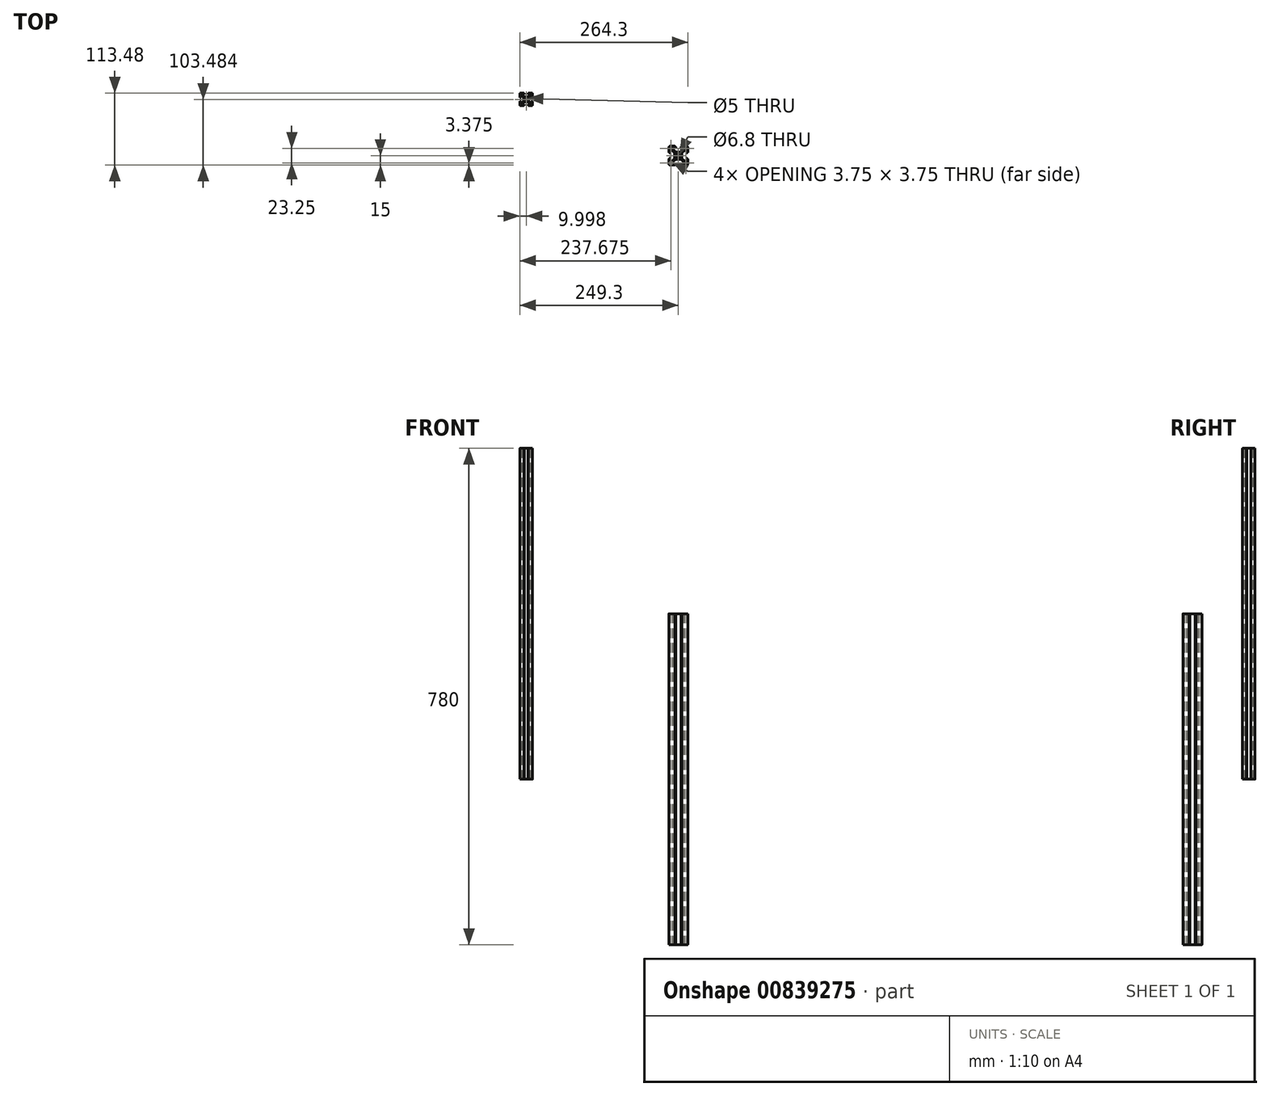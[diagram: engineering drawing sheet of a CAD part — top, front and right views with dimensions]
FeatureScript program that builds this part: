
annotation { "Feature Type Name" : "Feature", "Feature Type Description" : "" }
export const myFeature = defineFeature(function(context is Context, id is Id, definition is map)
    precondition{}
    {
        {
            var Q0;
            Q0=qCreatedBy(makeId("Top.planeOp"),FACE);
            var sketch = newSketch(context, id + "F0", { "sketchPlane" : qUnion([Q0])});
            skLineSegment(sketch, "E0.bottom", {"start": v(12.5, -15) * mm, "end": v(5.2, -15) * mm});
            skLineSegment(sketch, "E0.top", {"start": v(12.5, 15) * mm, "end": v(5.2, 15) * mm});
            skLineSegment(sketch, "E0.left", {"start": v(15, -12.5) * mm, "end": v(15, -5.2) * mm});
            skLineSegment(sketch, "E0.right", {"start": v(-15, -12.5) * mm, "end": v(-15, -5.2) * mm});
            skPoint(sketch, "E0.middle", {"position": v(0, 0) * mm});
            skCircle(sketch, "E1", {"center": v(0, 0) * mm, "radius": 3.4 * mm});
            skLineSegment(sketch, "E2.bottom", {"start": v(4.24, -5.8) * mm, "end": v(-4.24, -5.8) * mm});
            skLineSegment(sketch, "E2.top", {"start": v(4.24, 5.8) * mm, "end": v(-4.24, 5.8) * mm});
            skLineSegment(sketch, "E2.left", {"start": v(5.8, -4.24) * mm, "end": v(5.8, 4.24) * mm});
            skLineSegment(sketch, "E2.right", {"start": v(-5.8, -4.24) * mm, "end": v(-5.8, 4.24) * mm});
            skLineSegment(sketch, "E3.bottom", {"start": v(12.5, 15) * mm, "end": v(8.25, 15) * mm});
            skLineSegment(sketch, "E3.left", {"start": v(15, 12.5) * mm, "end": v(15, 8.25) * mm});
            skLineSegment(sketch, "E3.right", {"start": v(8.25, 12.8) * mm, "end": v(8.25, 9.8) * mm});
            skLineSegment(sketch, "E4.bottom", {"start": v(12.5, 9.75) * mm, "end": v(10.75, 9.75) * mm});
            skLineSegment(sketch, "E4.top", {"start": v(12.5, 13.5) * mm, "end": v(10.75, 13.5) * mm});
            skLineSegment(sketch, "E4.left", {"start": v(13.5, 10.75) * mm, "end": v(13.5, 12.5) * mm});
            skLineSegment(sketch, "E4.right", {"start": v(9.75, 10.75) * mm, "end": v(9.75, 12.5) * mm});
            skPoint(sketch, "E4.middle", {"position": v(11.62, 11.63) * mm});
            skLineSegment(sketch, "E5", {"start": v(9.8, 8.25) * mm, "end": v(5.8, 4.24) * mm});
            skLineSegment(sketch, "E6.MirrorCS", {"start": v(8.25, 9.8) * mm, "end": v(4.24, 5.8) * mm});
            skLineSegment(sketch, "E7", {"start": v(12.8, 8.25) * mm, "end": v(12.8, 4.1) * mm});
            skPoint(sketch, "E8.visualSharp", {"position": v(15, 15) * mm});
            skArc(sketch, "E8.filletArc", {"start": v(15, 12.5) * mm, "mid": v(14.27, 14.27) * mm, "end": v(12.5, 15) * mm});
            skLineSegment(sketch, "E9.MirrorCS", {"start": v(12.8, -8.25) * mm, "end": v(12.8, -4.1) * mm});
            skLineSegment(sketch, "E10", {"start": v(15, 8.25) * mm, "end": v(15, 5.2) * mm});
            skLineSegment(sketch, "E11", {"start": v(14.2, 5.2) * mm, "end": v(15, 5.2) * mm});
            skLineSegment(sketch, "E12", {"start": v(14, 5) * mm, "end": v(14, 4.1) * mm});
            skLineSegment(sketch, "E13", {"start": v(12.8, 4.1) * mm, "end": v(14, 4.1) * mm});
            skPoint(sketch, "E14.visualSharp", {"position": v(14, 5.2) * mm});
            skArc(sketch, "E14.filletArc", {"start": v(14.2, 5.2) * mm, "mid": v(14.06, 5.14) * mm, "end": v(14, 5) * mm});
            skLineSegment(sketch, "E15.MirrorCS", {"start": v(8.25, 12.8) * mm, "end": v(4.1, 12.8) * mm});
            skLineSegment(sketch, "E16.MirrorCS", {"start": v(4.1, 12.8) * mm, "end": v(4.1, 14) * mm});
            skLineSegment(sketch, "E17.MirrorCS", {"start": v(4.9, 14) * mm, "end": v(4.1, 14) * mm});
            skLineSegment(sketch, "E18.MirrorCS", {"start": v(5.2, 14.3) * mm, "end": v(5.2, 15) * mm});
            skArc(sketch, "E19.MirrorCS", {"start": v(5.2, 14.3) * mm, "mid": v(5.11, 14.09) * mm, "end": v(4.9, 14) * mm});
            skLineSegment(sketch, "E20.MirrorCS", {"start": v(8.25, -9.8) * mm, "end": v(4.24, -5.8) * mm});
            skLineSegment(sketch, "E21.MirrorCS", {"start": v(9.8, -8.25) * mm, "end": v(5.8, -4.24) * mm});
            skLineSegment(sketch, "E22.trimOffspring", {"start": v(12.8, 8.25) * mm, "end": v(9.8, 8.25) * mm});
            skLineSegment(sketch, "E23.MirrorCS", {"start": v(12.8, -8.25) * mm, "end": v(9.8, -8.25) * mm});
            skLineSegment(sketch, "E24.MirrorCS", {"start": v(12.5, -9.75) * mm, "end": v(10.75, -9.75) * mm});
            skLineSegment(sketch, "E25.MirrorCS", {"start": v(9.75, -10.75) * mm, "end": v(9.75, -12.5) * mm});
            skLineSegment(sketch, "E26.MirrorCS", {"start": v(13.5, -10.75) * mm, "end": v(13.5, -12.5) * mm});
            skLineSegment(sketch, "E27.MirrorCS", {"start": v(12.5, -13.5) * mm, "end": v(10.75, -13.5) * mm});
            skArc(sketch, "E28.MirrorCS", {"start": v(15, -12.5) * mm, "mid": v(14.27, -14.27) * mm, "end": v(12.5, -15) * mm});
            skLineSegment(sketch, "E29.MirrorCS", {"start": v(12.8, -4.1) * mm, "end": v(14, -4.1) * mm});
            skLineSegment(sketch, "E30.MirrorCS", {"start": v(14, -5) * mm, "end": v(14, -4.1) * mm});
            skLineSegment(sketch, "E31.MirrorCS", {"start": v(14.2, -5.2) * mm, "end": v(15, -5.2) * mm});
            skArc(sketch, "E32.MirrorCS", {"start": v(14.2, -5.2) * mm, "mid": v(14.06, -5.14) * mm, "end": v(14, -5) * mm});
            skLineSegment(sketch, "E33.MirrorCS", {"start": v(8.25, -12.8) * mm, "end": v(4.1, -12.8) * mm});
            skLineSegment(sketch, "E34.MirrorCS", {"start": v(4.1, -12.8) * mm, "end": v(4.1, -14) * mm});
            skArc(sketch, "E35.MirrorCS", {"start": v(5.2, -14.3) * mm, "mid": v(5.11, -14.09) * mm, "end": v(4.9, -14) * mm});
            skLineSegment(sketch, "E36.MirrorCS", {"start": v(5.2, -14.3) * mm, "end": v(5.2, -15) * mm});
            skLineSegment(sketch, "E37.MirrorCS", {"start": v(8.25, -12.8) * mm, "end": v(8.25, -9.8) * mm});
            skLineSegment(sketch, "E38.MirrorCS", {"start": v(4.9, -14) * mm, "end": v(4.1, -14) * mm});
            skPoint(sketch, "E39.orphan", {"position": v(15, -15) * mm});
            skLineSegment(sketch, "E40.trimOffspring", {"start": v(15, 5.2) * mm, "end": v(15, 12.5) * mm});
            skLineSegment(sketch, "E41.MirrorCS", {"start": v(-4.1, 12.8) * mm, "end": v(-4.1, 14) * mm});
            skLineSegment(sketch, "E42.MirrorCS", {"start": v(-4.9, 14) * mm, "end": v(-4.1, 14) * mm});
            skArc(sketch, "E43.MirrorCS", {"start": v(-5.2, 14.3) * mm, "mid": v(-5.11, 14.09) * mm, "end": v(-4.9, 14) * mm});
            skLineSegment(sketch, "E44.MirrorCS", {"start": v(-12.5, 13.5) * mm, "end": v(-10.75, 13.5) * mm});
            skLineSegment(sketch, "E45.MirrorCS", {"start": v(-8.25, 12.8) * mm, "end": v(-8.25, 9.8) * mm});
            skLineSegment(sketch, "E46.MirrorCS", {"start": v(-9.75, 10.75) * mm, "end": v(-9.75, 12.5) * mm});
            skPoint(sketch, "E47.MirrorP", {"position": v(-11.62, 11.63) * mm});
            skLineSegment(sketch, "E48.MirrorCS", {"start": v(-12.8, 8.25) * mm, "end": v(-9.8, 8.25) * mm});
            skLineSegment(sketch, "E49.MirrorCS", {"start": v(-13.5, 10.75) * mm, "end": v(-13.5, 12.5) * mm});
            skLineSegment(sketch, "E50.MirrorCS", {"start": v(-12.5, 9.75) * mm, "end": v(-10.75, 9.75) * mm});
            skLineSegment(sketch, "E51.MirrorCS", {"start": v(-8.25, 12.8) * mm, "end": v(-4.1, 12.8) * mm});
            skLineSegment(sketch, "E52.MirrorCS", {"start": v(-9.8, 8.25) * mm, "end": v(-5.8, 4.24) * mm});
            skLineSegment(sketch, "E53.MirrorCS", {"start": v(-8.25, 9.8) * mm, "end": v(-4.24, 5.8) * mm});
            skLineSegment(sketch, "E54.MirrorCS", {"start": v(-5.2, 14.3) * mm, "end": v(-5.2, 15) * mm});
            skLineSegment(sketch, "E55.MirrorCS", {"start": v(-14.2, 5.2) * mm, "end": v(-15, 5.2) * mm});
            skPoint(sketch, "E56.MirrorP", {"position": v(-14, 5.2) * mm});
            skArc(sketch, "E57.MirrorCS", {"start": v(-14.2, 5.2) * mm, "mid": v(-14.06, 5.14) * mm, "end": v(-14, 5) * mm});
            skLineSegment(sketch, "E58.MirrorCS", {"start": v(-14, 5) * mm, "end": v(-14, 4.1) * mm});
            skLineSegment(sketch, "E59.MirrorCS", {"start": v(-12.8, 8.25) * mm, "end": v(-12.8, 4.1) * mm});
            skLineSegment(sketch, "E60.MirrorCS", {"start": v(-12.8, 4.1) * mm, "end": v(-14, 4.1) * mm});
            skArc(sketch, "E61.MirrorCS", {"start": v(-15, 12.5) * mm, "mid": v(-14.27, 14.27) * mm, "end": v(-12.5, 15) * mm});
            skPoint(sketch, "E62.orphan", {"position": v(-15, 15) * mm});
            skLineSegment(sketch, "E63.trimOffspring", {"start": v(-5.2, 15) * mm, "end": v(-12.5, 15) * mm});
            skLineSegment(sketch, "E64.MirrorCS", {"start": v(-5.2, -14.3) * mm, "end": v(-5.2, -15) * mm});
            skLineSegment(sketch, "E65.MirrorCS", {"start": v(-4.9, -14) * mm, "end": v(-4.1, -14) * mm});
            skArc(sketch, "E66.MirrorCS", {"start": v(-5.2, -14.3) * mm, "mid": v(-5.11, -14.09) * mm, "end": v(-4.9, -14) * mm});
            skLineSegment(sketch, "E67.MirrorCS", {"start": v(-14, -5) * mm, "end": v(-14, -4.1) * mm});
            skLineSegment(sketch, "E68.MirrorCS", {"start": v(-4.1, -12.8) * mm, "end": v(-4.1, -14) * mm});
            skLineSegment(sketch, "E69.MirrorCS", {"start": v(-14.2, -5.2) * mm, "end": v(-15, -5.2) * mm});
            skArc(sketch, "E70.MirrorCS", {"start": v(-14.2, -5.2) * mm, "mid": v(-14.06, -5.14) * mm, "end": v(-14, -5) * mm});
            skLineSegment(sketch, "E71.MirrorCS", {"start": v(-12.8, -4.1) * mm, "end": v(-14, -4.1) * mm});
            skArc(sketch, "E72.MirrorCS", {"start": v(-15, -12.5) * mm, "mid": v(-14.27, -14.27) * mm, "end": v(-12.5, -15) * mm});
            skLineSegment(sketch, "E73.MirrorCS", {"start": v(-8.25, -12.8) * mm, "end": v(-8.25, -9.8) * mm});
            skLineSegment(sketch, "E74.MirrorCS", {"start": v(-8.25, -9.8) * mm, "end": v(-4.24, -5.8) * mm});
            skLineSegment(sketch, "E75.MirrorCS", {"start": v(-9.75, -10.75) * mm, "end": v(-9.75, -12.5) * mm});
            skLineSegment(sketch, "E76.MirrorCS", {"start": v(-8.25, -12.8) * mm, "end": v(-4.1, -12.8) * mm});
            skLineSegment(sketch, "E77.MirrorCS", {"start": v(-12.8, -8.25) * mm, "end": v(-12.8, -4.1) * mm});
            skLineSegment(sketch, "E78.MirrorCS", {"start": v(-12.8, -8.25) * mm, "end": v(-9.8, -8.25) * mm});
            skLineSegment(sketch, "E79.MirrorCS", {"start": v(-12.5, -9.75) * mm, "end": v(-10.75, -9.75) * mm});
            skLineSegment(sketch, "E80.MirrorCS", {"start": v(-12.5, -13.5) * mm, "end": v(-10.75, -13.5) * mm});
            skPoint(sketch, "E81.MirrorP", {"position": v(-15, -15) * mm});
            skLineSegment(sketch, "E82.MirrorCS", {"start": v(-9.8, -8.25) * mm, "end": v(-5.8, -4.24) * mm});
            skLineSegment(sketch, "E83.MirrorCS", {"start": v(-13.5, -10.75) * mm, "end": v(-13.5, -12.5) * mm});
            skLineSegment(sketch, "E84.trimOffspring", {"start": v(-5.2, -15) * mm, "end": v(-12.5, -15) * mm});
            skLineSegment(sketch, "E85.trimOffspring", {"start": v(-15, 5.2) * mm, "end": v(-15, 12.5) * mm});
            skPoint(sketch, "E86.orphan", {"position": v(5.8, 5.8) * mm});
            skPoint(sketch, "E87.orphan", {"position": v(-5.8, 5.8) * mm});
            skPoint(sketch, "E88.orphan", {"position": v(-5.8, -5.8) * mm});
            skPoint(sketch, "E89.orphan", {"position": v(5.8, -5.8) * mm});
            skPoint(sketch, "E90.visualSharp", {"position": v(13.5, 13.5) * mm});
            skArc(sketch, "E90.filletArc", {"start": v(13.5, 12.5) * mm, "mid": v(13.2, 13.2) * mm, "end": v(12.5, 13.5) * mm});
            skPoint(sketch, "E91.visualSharp", {"position": v(9.75, 13.5) * mm});
            skArc(sketch, "E91.filletArc", {"start": v(10.75, 13.5) * mm, "mid": v(10.04, 13.2) * mm, "end": v(9.75, 12.5) * mm});
            skPoint(sketch, "E92.visualSharp", {"position": v(9.75, 9.75) * mm});
            skArc(sketch, "E92.filletArc", {"start": v(9.75, 10.75) * mm, "mid": v(10.04, 10.04) * mm, "end": v(10.75, 9.75) * mm});
            skPoint(sketch, "E93.visualSharp", {"position": v(13.5, 9.75) * mm});
            skArc(sketch, "E93.filletArc", {"start": v(12.5, 9.75) * mm, "mid": v(13.2, 10.04) * mm, "end": v(13.5, 10.75) * mm});
            skArc(sketch, "E94.MirrorCS", {"start": v(9.75, -10.75) * mm, "mid": v(10.04, -10.04) * mm, "end": v(10.75, -9.75) * mm});
            skArc(sketch, "E95.MirrorCS", {"start": v(12.5, -9.75) * mm, "mid": v(13.2, -10.04) * mm, "end": v(13.5, -10.75) * mm});
            skArc(sketch, "E96.MirrorCS", {"start": v(10.75, -13.5) * mm, "mid": v(10.04, -13.2) * mm, "end": v(9.75, -12.5) * mm});
            skArc(sketch, "E97.MirrorCS", {"start": v(13.5, -12.5) * mm, "mid": v(13.2, -13.2) * mm, "end": v(12.5, -13.5) * mm});
            skArc(sketch, "E98.MirrorCS", {"start": v(-10.75, 13.5) * mm, "mid": v(-10.04, 13.2) * mm, "end": v(-9.75, 12.5) * mm});
            skArc(sketch, "E99.MirrorCS", {"start": v(-9.75, 10.75) * mm, "mid": v(-10.04, 10.04) * mm, "end": v(-10.75, 9.75) * mm});
            skArc(sketch, "E100.MirrorCS", {"start": v(-12.5, 9.75) * mm, "mid": v(-13.2, 10.04) * mm, "end": v(-13.5, 10.75) * mm});
            skArc(sketch, "E101.MirrorCS", {"start": v(-13.5, 12.5) * mm, "mid": v(-13.2, 13.2) * mm, "end": v(-12.5, 13.5) * mm});
            skArc(sketch, "E102.MirrorCS", {"start": v(-9.75, -10.75) * mm, "mid": v(-10.04, -10.04) * mm, "end": v(-10.75, -9.75) * mm});
            skArc(sketch, "E103.MirrorCS", {"start": v(-12.5, -9.75) * mm, "mid": v(-13.2, -10.04) * mm, "end": v(-13.5, -10.75) * mm});
            skArc(sketch, "E104.MirrorCS", {"start": v(-13.5, -12.5) * mm, "mid": v(-13.2, -13.2) * mm, "end": v(-12.5, -13.5) * mm});
            skArc(sketch, "E105.MirrorCS", {"start": v(-10.75, -13.5) * mm, "mid": v(-10.04, -13.2) * mm, "end": v(-9.75, -12.5) * mm});
            skPoint(sketch, "E106.orphan", {"position": v(13.5, -9.75) * mm});
            skPoint(sketch, "E107.orphan", {"position": v(9.75, -9.75) * mm});
            skPoint(sketch, "E108.orphan", {"position": v(9.75, -13.5) * mm});
            skPoint(sketch, "E109.orphan", {"position": v(13.5, -13.5) * mm});
            skPoint(sketch, "E110.orphan", {"position": v(-13.5, -9.75) * mm});
            skPoint(sketch, "E111.orphan", {"position": v(-9.75, -9.75) * mm});
            skPoint(sketch, "E112.orphan", {"position": v(-9.75, -13.5) * mm});
            skPoint(sketch, "E113.orphan", {"position": v(-13.5, -13.5) * mm});
            skPoint(sketch, "E114.orphan", {"position": v(-9.75, 13.5) * mm});
            skPoint(sketch, "E115.orphan", {"position": v(-13.5, 13.5) * mm});
            skPoint(sketch, "E116.orphan", {"position": v(-13.5, 9.75) * mm});
            skPoint(sketch, "E117.orphan", {"position": v(-9.75, 9.75) * mm});
            skSolve(sketch);
        }
        {
            var Q0;
            Q0=makeQuery(id+"F0.imprint","IMPRINT",FACE,{"disambiguationData":[TD([[makeQuery(id+"F0.imprint","IMPRINT",EDGE,{"derivedFrom":sQuery(id+"F0.wireOp",EDGE,"E0.bottom")}),-1.0]])]});
            extrude(context, id + "F1", {"entities" : qUnion([Q0]), "endBound" : BoundingType.SYMMETRIC, "depth" : 520 * mm, "offsetDistance" : 25 * mm});
        }
        {
            var Q0;
            Q0=qCreatedBy(makeId("Top.planeOp"),FACE);
            var sketch = newSketch(context, id + "F2", { "sketchPlane" : qUnion([Q0])});
            skCircle(sketch, "E118", {"center": v(-239.3, 88.48) * mm, "radius": 2.5 * mm});
            skLineSegment(sketch, "E119.bottom", {"start": v(-230.8, 78.48) * mm, "end": v(-235.2, 78.48) * mm});
            skLineSegment(sketch, "E119.top", {"start": v(-230.8, 98.48) * mm, "end": v(-235.2, 98.48) * mm});
            skLineSegment(sketch, "E119.left", {"start": v(-229.3, 79.98) * mm, "end": v(-229.3, 84.88) * mm});
            skLineSegment(sketch, "E120.bottom", {"start": v(-237.3, 84.58) * mm, "end": v(-241.31, 84.58) * mm});
            skLineSegment(sketch, "E120.top", {"start": v(-237.3, 92.38) * mm, "end": v(-241.31, 92.38) * mm});
            skLineSegment(sketch, "E120.left", {"start": v(-235.4, 86.47) * mm, "end": v(-235.4, 90.5) * mm});
            skLineSegment(sketch, "E120.right", {"start": v(-243.2, 86.47) * mm, "end": v(-243.2, 90.5) * mm});
            skLineSegment(sketch, "E121.bottom", {"start": v(-230.8, 98.48) * mm, "end": v(-233.8, 98.48) * mm});
            skLineSegment(sketch, "E121.left", {"start": v(-229.3, 96.98) * mm, "end": v(-229.3, 93.98) * mm});
            skLineSegment(sketch, "E121.right", {"start": v(-233.8, 96.68) * mm, "end": v(-233.8, 95.04) * mm});
            skLineSegment(sketch, "E122", {"start": v(-234.82, 91.9) * mm, "end": v(-232.74, 93.98) * mm});
            skLineSegment(sketch, "E123.MirrorCS", {"start": v(-235.88, 92.97) * mm, "end": v(-233.8, 95.04) * mm});
            skLineSegment(sketch, "E124", {"start": v(-231.1, 93.98) * mm, "end": v(-231.1, 91.58) * mm});
            skLineSegment(sketch, "E125", {"start": v(-229.6, 92.08) * mm, "end": v(-229.3, 92.08) * mm});
            skLineSegment(sketch, "E126", {"start": v(-231.1, 91.58) * mm, "end": v(-229.8, 91.58) * mm});
            skLineSegment(sketch, "E127", {"start": v(-229.8, 91.88) * mm, "end": v(-229.8, 91.58) * mm});
            skPoint(sketch, "E128.visualSharp", {"position": v(-229.8, 92.08) * mm});
            skArc(sketch, "E128.filletArc", {"start": v(-229.6, 92.08) * mm, "mid": v(-229.74, 92.03) * mm, "end": v(-229.8, 91.88) * mm});
            skPoint(sketch, "E129.newPointA", {"position": v(-235.4, 91.32) * mm});
            skArc(sketch, "E129.filletArc", {"start": v(-234.82, 91.9) * mm, "mid": v(-235.25, 91.26) * mm, "end": v(-235.4, 90.5) * mm});
            skPoint(sketch, "E130.newPointA", {"position": v(-236.46, 92.38) * mm});
            skPoint(sketch, "E130.newPointB", {"position": v(-235.4, 92.38) * mm});
            skArc(sketch, "E130.filletArc", {"start": v(-237.3, 92.38) * mm, "mid": v(-236.53, 92.54) * mm, "end": v(-235.88, 92.97) * mm});
            skLineSegment(sketch, "E131.MirrorCS", {"start": v(-233.8, 96.68) * mm, "end": v(-236.2, 96.68) * mm});
            skLineSegment(sketch, "E132.MirrorCS", {"start": v(-236.2, 96.68) * mm, "end": v(-236.2, 97.98) * mm});
            skPoint(sketch, "E133.visualSharp", {"position": v(-229.3, 98.48) * mm});
            skArc(sketch, "E133.filletArc", {"start": v(-229.3, 96.98) * mm, "mid": v(-229.74, 98.04) * mm, "end": v(-230.8, 98.48) * mm});
            skLineSegment(sketch, "E134.trimOffspring", {"start": v(-231.1, 93.98) * mm, "end": v(-232.74, 93.98) * mm});
            skLineSegment(sketch, "E135.MirrorCS", {"start": v(-229.6, 84.88) * mm, "end": v(-229.3, 84.88) * mm});
            skArc(sketch, "E136.MirrorCS", {"start": v(-229.6, 84.88) * mm, "mid": v(-229.74, 84.94) * mm, "end": v(-229.8, 85.08) * mm});
            skLineSegment(sketch, "E137.MirrorCS", {"start": v(-229.8, 85.08) * mm, "end": v(-229.8, 85.38) * mm});
            skArc(sketch, "E138.MirrorCS", {"start": v(-234.82, 85.06) * mm, "mid": v(-235.25, 85.7) * mm, "end": v(-235.4, 86.47) * mm});
            skLineSegment(sketch, "E139.MirrorCS", {"start": v(-231.1, 82.98) * mm, "end": v(-232.74, 82.98) * mm});
            skLineSegment(sketch, "E140.MirrorCS", {"start": v(-231.1, 85.38) * mm, "end": v(-229.8, 85.38) * mm});
            skLineSegment(sketch, "E141.MirrorCS", {"start": v(-230.8, 78.48) * mm, "end": v(-233.8, 78.48) * mm});
            skPoint(sketch, "E142.MirrorP", {"position": v(-229.8, 84.88) * mm});
            skLineSegment(sketch, "E143.MirrorCS", {"start": v(-236.2, 80.28) * mm, "end": v(-236.2, 78.98) * mm});
            skLineSegment(sketch, "E144.MirrorCS", {"start": v(-233.8, 80.28) * mm, "end": v(-236.2, 80.28) * mm});
            skLineSegment(sketch, "E145.MirrorCS", {"start": v(-231.1, 82.98) * mm, "end": v(-231.1, 85.38) * mm});
            skLineSegment(sketch, "E146.MirrorCS", {"start": v(-229.3, 79.98) * mm, "end": v(-229.3, 82.98) * mm});
            skLineSegment(sketch, "E147.MirrorCS", {"start": v(-234.82, 85.06) * mm, "end": v(-232.74, 82.98) * mm});
            skPoint(sketch, "E148.MirrorP", {"position": v(-235.4, 85.64) * mm});
            skPoint(sketch, "E149.MirrorP", {"position": v(-229.3, 78.48) * mm});
            skPoint(sketch, "E150.MirrorP", {"position": v(-235.4, 84.58) * mm});
            skLineSegment(sketch, "E151.MirrorCS", {"start": v(-235.88, 84) * mm, "end": v(-233.8, 81.92) * mm});
            skPoint(sketch, "E152.MirrorP", {"position": v(-236.46, 84.58) * mm});
            skArc(sketch, "E153.MirrorCS", {"start": v(-229.3, 79.98) * mm, "mid": v(-229.74, 78.92) * mm, "end": v(-230.8, 78.48) * mm});
            skLineSegment(sketch, "E154.MirrorCS", {"start": v(-233.8, 80.28) * mm, "end": v(-233.8, 81.92) * mm});
            skArc(sketch, "E155.MirrorCS", {"start": v(-237.3, 84.58) * mm, "mid": v(-236.53, 84.43) * mm, "end": v(-235.88, 84) * mm});
            skLineSegment(sketch, "E156.trimOffspring", {"start": v(-229.3, 92.08) * mm, "end": v(-229.3, 96.98) * mm});
            skLineSegment(sketch, "E157.MirrorCS", {"start": v(-235.7, 98.18) * mm, "end": v(-235.7, 98.48) * mm});
            skArc(sketch, "E158.MirrorCS", {"start": v(-235.7, 98.18) * mm, "mid": v(-235.76, 98.04) * mm, "end": v(-235.9, 97.98) * mm});
            skLineSegment(sketch, "E159.MirrorCS", {"start": v(-235.9, 97.98) * mm, "end": v(-236.2, 97.98) * mm});
            skLineSegment(sketch, "E160", {"start": v(-235.2, 98.48) * mm, "end": v(-235.7, 98.48) * mm});
            skLineSegment(sketch, "E161.MirrorCS", {"start": v(-235.7, 78.78) * mm, "end": v(-235.7, 78.48) * mm});
            skLineSegment(sketch, "E162.MirrorCS", {"start": v(-235.9, 78.98) * mm, "end": v(-236.2, 78.98) * mm});
            skLineSegment(sketch, "E163.MirrorCS", {"start": v(-235.2, 78.48) * mm, "end": v(-235.7, 78.48) * mm});
            skArc(sketch, "E164.MirrorCS", {"start": v(-235.7, 78.78) * mm, "mid": v(-235.76, 78.93) * mm, "end": v(-235.9, 78.98) * mm});
            skArc(sketch, "E165.MirrorCS", {"start": v(-249, 84.88) * mm, "mid": v(-248.86, 84.94) * mm, "end": v(-248.8, 85.08) * mm});
            skLineSegment(sketch, "E166.MirrorCS", {"start": v(-249, 92.08) * mm, "end": v(-249.3, 92.08) * mm});
            skLineSegment(sketch, "E167.MirrorCS", {"start": v(-248.8, 85.08) * mm, "end": v(-248.8, 85.38) * mm});
            skArc(sketch, "E168.MirrorCS", {"start": v(-249, 92.08) * mm, "mid": v(-248.86, 92.03) * mm, "end": v(-248.8, 91.88) * mm});
            skLineSegment(sketch, "E169.MirrorCS", {"start": v(-248.8, 91.88) * mm, "end": v(-248.8, 91.58) * mm});
            skLineSegment(sketch, "E170.MirrorCS", {"start": v(-249, 84.88) * mm, "end": v(-249.3, 84.88) * mm});
            skLineSegment(sketch, "E171.MirrorCS", {"start": v(-243.4, 98.48) * mm, "end": v(-242.9, 98.48) * mm});
            skArc(sketch, "E172.MirrorCS", {"start": v(-249.3, 79.98) * mm, "mid": v(-248.86, 78.92) * mm, "end": v(-247.8, 78.48) * mm});
            skLineSegment(sketch, "E173.MirrorCS", {"start": v(-242.9, 98.18) * mm, "end": v(-242.9, 98.48) * mm});
            skArc(sketch, "E174.MirrorCS", {"start": v(-243.79, 91.9) * mm, "mid": v(-243.35, 91.26) * mm, "end": v(-243.2, 90.5) * mm});
            skLineSegment(sketch, "E175.MirrorCS", {"start": v(-242.7, 78.98) * mm, "end": v(-242.4, 78.98) * mm});
            skLineSegment(sketch, "E176.MirrorCS", {"start": v(-242.4, 96.68) * mm, "end": v(-242.4, 97.98) * mm});
            skLineSegment(sketch, "E177.MirrorCS", {"start": v(-241.31, 92.38) * mm, "end": v(-237.3, 92.38) * mm});
            skLineSegment(sketch, "E178.MirrorCS", {"start": v(-247.5, 85.38) * mm, "end": v(-248.8, 85.38) * mm});
            skLineSegment(sketch, "E179.MirrorCS", {"start": v(-247.5, 91.58) * mm, "end": v(-248.8, 91.58) * mm});
            skLineSegment(sketch, "E180.MirrorCS", {"start": v(-242.7, 97.98) * mm, "end": v(-242.4, 97.98) * mm});
            skArc(sketch, "E181.MirrorCS", {"start": v(-243.79, 85.06) * mm, "mid": v(-243.35, 85.7) * mm, "end": v(-243.2, 86.47) * mm});
            skArc(sketch, "E182.MirrorCS", {"start": v(-242.9, 78.78) * mm, "mid": v(-242.84, 78.93) * mm, "end": v(-242.7, 78.98) * mm});
            skArc(sketch, "E183.MirrorCS", {"start": v(-242.9, 98.18) * mm, "mid": v(-242.84, 98.04) * mm, "end": v(-242.7, 97.98) * mm});
            skLineSegment(sketch, "E184.MirrorCS", {"start": v(-242.9, 78.78) * mm, "end": v(-242.9, 78.48) * mm});
            skLineSegment(sketch, "E185.MirrorCS", {"start": v(-241.31, 84.58) * mm, "end": v(-237.3, 84.58) * mm});
            skLineSegment(sketch, "E186.MirrorCS", {"start": v(-243.4, 78.48) * mm, "end": v(-242.9, 78.48) * mm});
            skLineSegment(sketch, "E187.MirrorCS", {"start": v(-242.4, 80.28) * mm, "end": v(-242.4, 78.98) * mm});
            skArc(sketch, "E188.MirrorCS", {"start": v(-241.31, 92.38) * mm, "mid": v(-242.08, 92.54) * mm, "end": v(-242.73, 92.97) * mm});
            skPoint(sketch, "E189.MirrorP", {"position": v(-249.3, 78.48) * mm});
            skLineSegment(sketch, "E190.MirrorCS", {"start": v(-247.8, 78.48) * mm, "end": v(-243.4, 78.48) * mm});
            skPoint(sketch, "E191.MirrorP", {"position": v(-243.2, 84.58) * mm});
            skLineSegment(sketch, "E192.MirrorCS", {"start": v(-247.8, 98.48) * mm, "end": v(-243.4, 98.48) * mm});
            skArc(sketch, "E193.MirrorCS", {"start": v(-241.31, 84.58) * mm, "mid": v(-242.08, 84.43) * mm, "end": v(-242.73, 84) * mm});
            skArc(sketch, "E194.MirrorCS", {"start": v(-249.3, 96.98) * mm, "mid": v(-248.86, 98.04) * mm, "end": v(-247.8, 98.48) * mm});
            skPoint(sketch, "E195.MirrorP", {"position": v(-243.2, 85.64) * mm});
            skLineSegment(sketch, "E196.MirrorCS", {"start": v(-244.8, 96.68) * mm, "end": v(-244.8, 95.04) * mm});
            skLineSegment(sketch, "E197.MirrorCS", {"start": v(-242.73, 92.97) * mm, "end": v(-244.8, 95.04) * mm});
            skPoint(sketch, "E198.MirrorP", {"position": v(-243.2, 91.32) * mm});
            skLineSegment(sketch, "E199.MirrorCS", {"start": v(-247.5, 82.98) * mm, "end": v(-247.5, 85.38) * mm});
            skLineSegment(sketch, "E200.MirrorCS", {"start": v(-243.79, 85.06) * mm, "end": v(-245.86, 82.98) * mm});
            skLineSegment(sketch, "E201.MirrorCS", {"start": v(-244.8, 80.28) * mm, "end": v(-242.4, 80.28) * mm});
            skLineSegment(sketch, "E202.MirrorCS", {"start": v(-247.5, 82.98) * mm, "end": v(-245.86, 82.98) * mm});
            skLineSegment(sketch, "E203.MirrorCS", {"start": v(-249.3, 79.98) * mm, "end": v(-249.3, 82.98) * mm});
            skLineSegment(sketch, "E204.MirrorCS", {"start": v(-247.8, 98.48) * mm, "end": v(-244.8, 98.48) * mm});
            skLineSegment(sketch, "E205.MirrorCS", {"start": v(-249.3, 92.08) * mm, "end": v(-249.3, 96.98) * mm});
            skLineSegment(sketch, "E206.MirrorCS", {"start": v(-244.8, 96.68) * mm, "end": v(-242.4, 96.68) * mm});
            skLineSegment(sketch, "E207.MirrorCS", {"start": v(-242.73, 84) * mm, "end": v(-244.8, 81.92) * mm});
            skPoint(sketch, "E208.MirrorP", {"position": v(-242.14, 84.58) * mm});
            skLineSegment(sketch, "E209.MirrorCS", {"start": v(-247.5, 93.98) * mm, "end": v(-247.5, 91.58) * mm});
            skLineSegment(sketch, "E210.MirrorCS", {"start": v(-249.3, 96.98) * mm, "end": v(-249.3, 93.98) * mm});
            skPoint(sketch, "E211.MirrorP", {"position": v(-248.8, 84.88) * mm});
            skPoint(sketch, "E212.MirrorP", {"position": v(-249.3, 98.48) * mm});
            skPoint(sketch, "E213.MirrorP", {"position": v(-248.8, 92.08) * mm});
            skLineSegment(sketch, "E214.MirrorCS", {"start": v(-243.79, 91.9) * mm, "end": v(-245.86, 93.98) * mm});
            skLineSegment(sketch, "E215.MirrorCS", {"start": v(-247.5, 93.98) * mm, "end": v(-245.86, 93.98) * mm});
            skLineSegment(sketch, "E216.MirrorCS", {"start": v(-249.3, 79.98) * mm, "end": v(-249.3, 84.88) * mm});
            skLineSegment(sketch, "E217.MirrorCS", {"start": v(-247.8, 78.48) * mm, "end": v(-244.8, 78.48) * mm});
            skPoint(sketch, "E218.MirrorP", {"position": v(-243.2, 92.38) * mm});
            skPoint(sketch, "E219.MirrorP", {"position": v(-242.14, 92.38) * mm});
            skLineSegment(sketch, "E220.MirrorCS", {"start": v(-244.8, 80.28) * mm, "end": v(-244.8, 81.92) * mm});
            skSolve(sketch);
        }
        {
            var Q0;
            Q0=makeQuery(id+"F2.imprint","IMPRINT",FACE,{"disambiguationData":[TD([[makeQuery(id+"F2.imprint","IMPRINT",EDGE,{"derivedFrom":sQuery(id+"F2.wireOp",EDGE,"E119.bottom")}),-1.0]])]});
            extrude(context, id + "F3", {"entities" : qUnion([Q0]), "depth" : 520 * mm, "offsetDistance" : 25 * mm});
        }
    });
